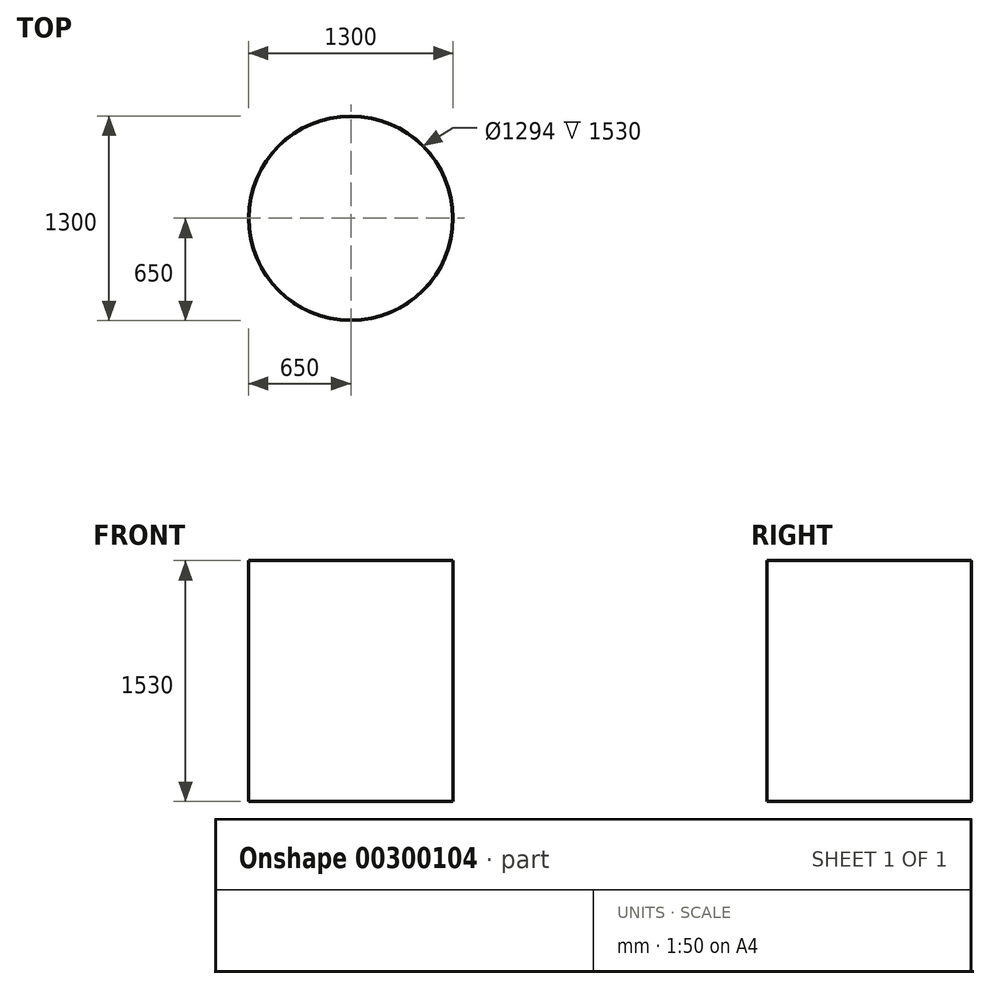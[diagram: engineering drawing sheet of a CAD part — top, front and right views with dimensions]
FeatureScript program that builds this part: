
annotation { "Feature Type Name" : "Feature", "Feature Type Description" : "" }
export const myFeature = defineFeature(function(context is Context, id is Id, definition is map)
    precondition{}
    {
        {
            var Q0;
            Q0=qCreatedBy(makeId("Top.planeOp"),FACE);
            var sketch = newSketch(context, id + "F0", { "sketchPlane" : qUnion([Q0])});
            skCircle(sketch, "E0", {"center": v(0, 0) * mm, "radius": 650 * mm});
            skCircle(sketch, "E1.0", {"center": v(0, 0) * mm, "radius": 647 * mm});
            skSolve(sketch);
        }
        {
            var Q0;
            Q0 = qSketchRegion(id + "F0", true);
            extrude(context, id + "F1", {"entities" : qUnion([Q0]), "depth" : 1530 * mm});
        }
    });
